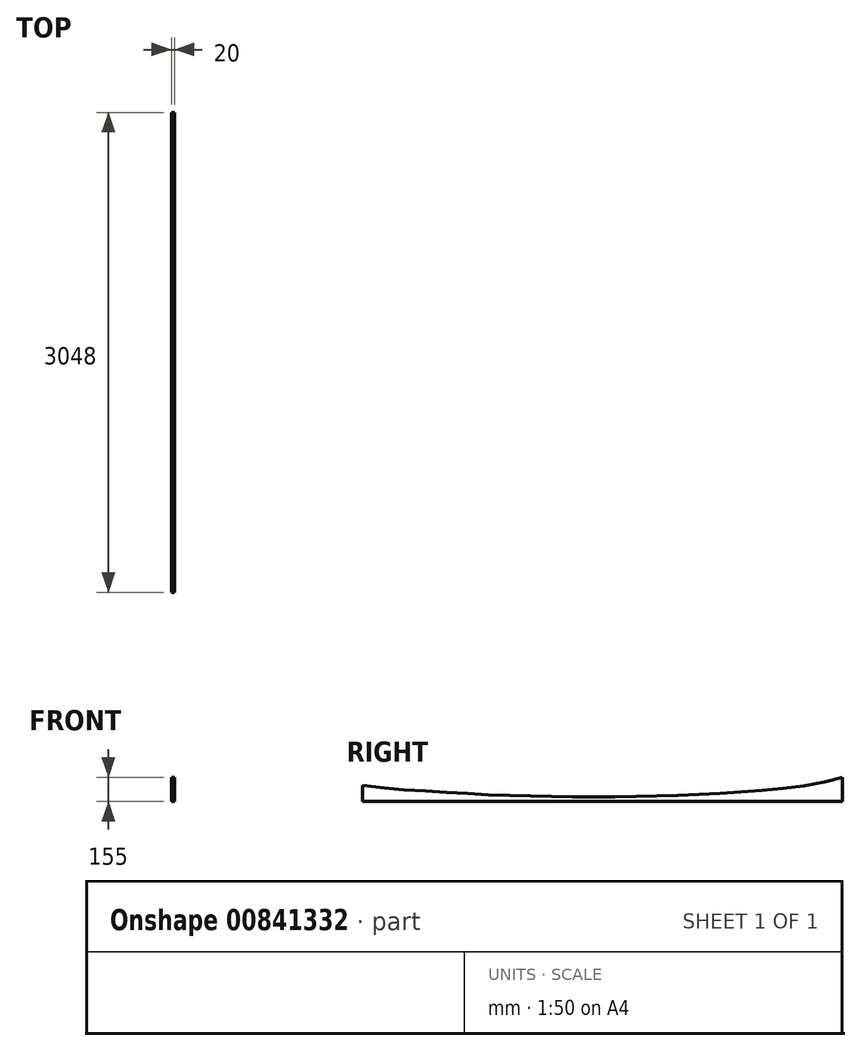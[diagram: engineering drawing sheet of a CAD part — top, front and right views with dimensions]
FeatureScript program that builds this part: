
annotation { "Feature Type Name" : "Feature", "Feature Type Description" : "" }
export const myFeature = defineFeature(function(context is Context, id is Id, definition is map)
    precondition{}
    {
        {
            var Q0;
            Q0=qCreatedBy(makeId("Right.planeOp"),FACE);
            var sketch = newSketch(context, id + "F0", { "sketchPlane" : qUnion([Q0])});
            skLineSegment(sketch, "E0", {"start": v(-1524, 0) * mm, "end": v(-1524, 102) * mm});
            skFitSpline(sketch, "E1", {"points": [v(-1524, 102) * mm, v(-1424, 91) * mm, v(-1324, 81) * mm, v(-1224, 73) * mm, v(-1124, 67) * mm, v(-1024, 60) * mm, v(-924, 54) * mm, v(-824, 49) * mm, v(-724, 44) * mm, v(-624, 40) * mm, v(-524, 37) * mm, v(-424, 34) * mm, v(-324, 32) * mm, v(-224, 31) * mm, v(-124, 30) * mm, v(-24, 30) * mm, v(76, 30) * mm, v(176, 31) * mm, v(276, 33) * mm, v(376, 36) * mm, v(476, 39) * mm, v(576, 43) * mm, v(676, 48) * mm, v(776, 54) * mm, v(876, 60) * mm, v(976, 68) * mm, v(1076, 77) * mm, v(1176, 87) * mm, v(1276, 100) * mm, v(1376, 116) * mm, v(1476, 140) * mm, v(1524, 155) * mm], "startDerivative": vector(44.76, -10.57) * mm, "endDerivative": vector(60.2, 24.67) * mm});
            skLineSegment(sketch, "E2", {"start": v(-1524, 30) * mm, "end": v(1524, 30) * mm, "construction": true});
            skLineSegment(sketch, "E3", {"start": v(1524, 155) * mm, "end": v(1523.54, 154.81) * mm, "construction": true});
            skPoint(sketch, "E4", {"position": v(1219, 30) * mm});
            skPoint(sketch, "E5", {"position": v(-1219, 30) * mm});
            skLineSegment(sketch, "E6", {"start": v(-1524, 102) * mm, "end": v(-1523.51, 101.89) * mm, "construction": true});
            skLineSegment(sketch, "E7", {"start": v(-1524, 0) * mm, "end": v(1524, 0) * mm});
            skLineSegment(sketch, "E8", {"start": v(1524, 0) * mm, "end": v(1524, 155) * mm});
            skSolve(sketch);
        }
        {
            var Q0;
            Q0=qSketchRegion(id+"F0",true);
            extrude(context, id + "F1", {"entities" : qUnion([Q0]), "depth" : 20 * mm, "offsetDistance" : 25 * mm});
        }
    });
